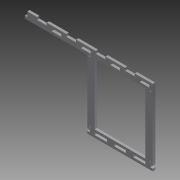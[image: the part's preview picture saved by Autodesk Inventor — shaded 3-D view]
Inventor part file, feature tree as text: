
AUTODESK INVENTOR PART (.ipt)
format: ipt  version: 2011 (Build 150239000, 239)  size: 552,960 bytes
history: native  units: in
note: dims shown in document units (in); Inventor stores cm internally (conversion verified against a paired STEP export)
features: extrude x19, sketch x19
ambient origin geometry x8: Origin, YZ Plane, XZ Plane, XY Plane, X Axis, Y Axis, Z Axis, Center Point
bodies: Solid1 (feature_tree)
feature tree (38):
  extrude  "Extrusion1"  Depth=6.75in
  extrude  "Extrusion2"  Depth=0.5in
  extrude  "Extrusion3"  Depth=0.5in
  extrude  "Extrusion4"  Depth=5.75in
  extrude  "Extrusion5"  Depth=0.5in
  extrude  "Extrusion6"  Depth=1.5in
  extrude  "Extrusion7"  Depth=1.5in
  extrude  "Extrusion8"  Depth=0.156in
  extrude  "Extrusion9"  Depth=0.25in TaperAngle=0.0deg
  extrude  "Extrusion10"  Depth=0.25in TaperAngle=0.0deg
  extrude  "Extrusion11"  Depth=0.25in TaperAngle=0.0deg
  extrude  "Extrusion12"  Depth=0.25in
  extrude  "Extrusion13"  Depth=0.25in
  extrude  "Extrusion14"  Depth=0.25in TaperAngle=0.0deg
  extrude  "Extrusion15"  Depth=3.0in
  extrude  "Extrusion16"  Depth=0.25in TaperAngle=0.0deg
  extrude  "Extrusion17"  Depth=1.0in
  extrude  "Extrusion18"  Depth=0.25in TaperAngle=0.0deg
  extrude  "Extrusion19"  Depth=0.25in TaperAngle=0.0deg
  sketch  "Sketch1"  dims[d0=5.2in d1=6.75in]
  sketch  "Sketch2"  dims[d2=0.25in d3=0.5in]
  sketch  "Sketch3"  dims[d4=5.7in d5=0.5in]
  sketch  "Sketch4"  dims[d6=0.5in d7=5.75in]
  sketch  "Sketch5"  dims[d8=0.375in d9=0.5in]
  sketch  "Sketch6"  dims[d10=0.25in d11=1.5in]
  sketch  "Sketch7"  dims[d12=0.25in d13=1.5in]
  sketch  "Sketch8"  dims[d14=0.25in d15=0.156in]
  sketch  "Sketch9"  dims[d16=0.156in d17=0.25in d18=0.0in]
  sketch  "Sketch10"  dims[d19=0.125in d20=0.0in d21=0.25in d22=0.0in]
  sketch  "Sketch11"  dims[d23=0.25in d24=0.0in d25=0.25in d26=0.0in]
  sketch  "Sketch12"  dims[d27=0.25in d28=0.25in]
  sketch  "Sketch13"  dims[d29=0.25in d30=0.25in]
  sketch  "Sketch14"  dims[d31=0.25in d32=0.25in d33=0.0in]
  sketch  "Sketch15"  dims[d34=1.5in d35=3.0in]
  sketch  "Sketch16"  dims[d36=1.0in d37=0.25in d38=0.0in]
  sketch  "Sketch17"  dims[d39=6.65in d40=1.0in]
  sketch  "Sketch18"  dims[d41=1.5in d42=0.25in d43=0.0in]
  sketch  "Sketch19"  dims[d44=0.25in d45=0.0in d46=0.25in d47=0.0in d48=1.0in d49=0.25in d50=0.0in d51=0.25in d52=1.0in d53=0.25in d54=1.0in d55=0.25in d56=2.0in d57=1.0in d58=0.5in d59=1.0in d60=0.5in d61=1.0in d62=0.5in d63=1.0in d64=0.5in d65=1.0in d66=0.5in d67=1.0in d68=0.5in d69=1.0in d70=0.25in d71=0.0in d72=0.25in d73=1.0in d74=1.0in d75=0.25in d76=0.0in d77=0.25in d78=0.0in d79=0.25in d80=0.25in d81=0.0in d82=0.75in d83=0.156in d84=0.156in d85=0.25in d86=0.0in d87=0.25in d88=0.0in d89=1.0in d90=1.0in d91=1.0in d92=0.25in d93=0.0in d94=1.0in d95=0.0in]
